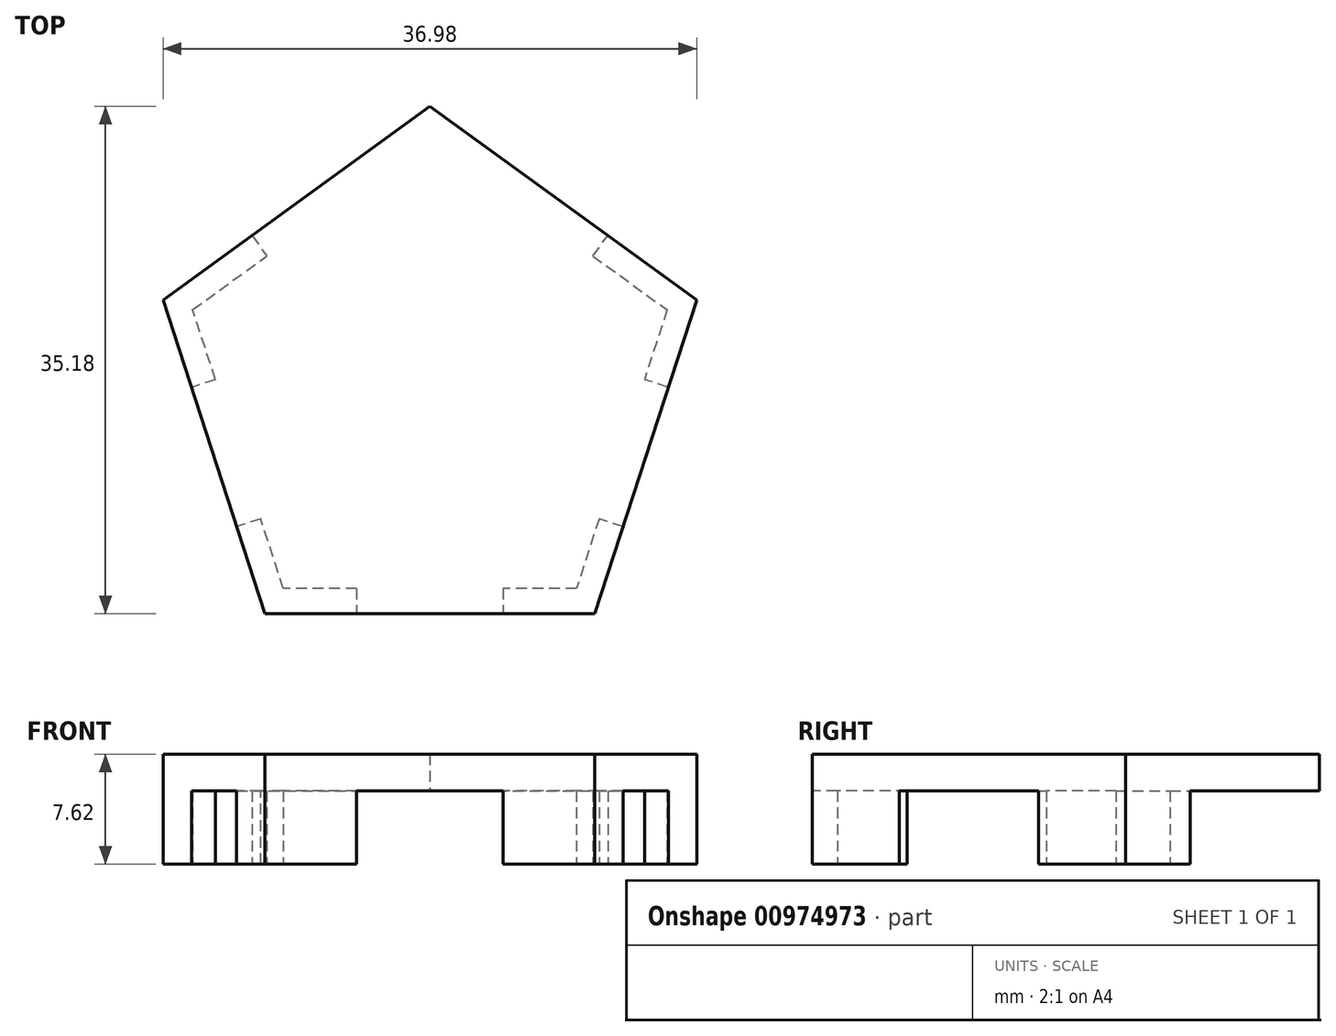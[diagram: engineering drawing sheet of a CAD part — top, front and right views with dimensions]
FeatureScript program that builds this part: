
annotation { "Feature Type Name" : "Feature", "Feature Type Description" : "" }
export const myFeature = defineFeature(function(context is Context, id is Id, definition is map)
    precondition{}
    {
        {
            var Q0;
            Q0=qCreatedBy(makeId("Top.planeOp"),FACE);
            var sketch = newSketch(context, id + "F0", { "sketchPlane" : qUnion([Q0])});
            skCircle(sketch, "E0.cCircle", {"center": v(0, 0) * mm, "radius": 19.45 * mm, "construction": true});
            skLineSegment(sketch, "E0.0", {"start": v(11.43, -15.73) * mm, "end": v(-11.43, -15.73) * mm});
            skLineSegment(sketch, "E0.1", {"start": v(-11.43, -15.73) * mm, "end": v(-18.5, 6) * mm});
            skLineSegment(sketch, "E0.2", {"start": v(-18.5, 6) * mm, "end": v(0, 19.45) * mm});
            skLineSegment(sketch, "E0.3", {"start": v(0, 19.45) * mm, "end": v(18.5, 6) * mm});
            skLineSegment(sketch, "E0.4", {"start": v(18.5, 6) * mm, "end": v(11.43, -15.73) * mm});
            skSolve(sketch);
        }
        {
            var Q0;
            Q0=makeQuery(id+"F0.imprint","IMPRINT",FACE,{"disambiguationData":[TD([[makeQuery(id+"F0.imprint","IMPRINT",EDGE,{"derivedFrom":sQuery(id+"F0.wireOp",EDGE,"E0.0")}),-1.0]])]});
            extrude(context, id + "F1", {"entities" : qUnion([Q0]), "depth" : 7.62 * mm, "offsetDistance" : 25.4 * mm});
        }
        {
            var Q0;
            Q0=qCreatedBy(makeId("Top.planeOp"),FACE);
            var sketch = newSketch(context, id + "F2", { "sketchPlane" : qUnion([Q0])});
            skCircle(sketch, "E1.cCircle", {"center": v(0, 0) * mm, "radius": 13.98 * mm, "construction": true});
            skLineSegment(sketch, "E1.0", {"start": v(16.44, 5.34) * mm, "end": v(10.16, -13.98) * mm});
            skLineSegment(sketch, "E1.1", {"start": v(10.16, -13.98) * mm, "end": v(-10.16, -13.98) * mm});
            skLineSegment(sketch, "E1.2", {"start": v(-10.16, -13.98) * mm, "end": v(-16.44, 5.34) * mm});
            skLineSegment(sketch, "E1.3", {"start": v(-16.44, 5.34) * mm, "end": v(0, 17.29) * mm});
            skLineSegment(sketch, "E1.4", {"start": v(0, 17.29) * mm, "end": v(16.44, 5.34) * mm});
            skPoint(sketch, "E1.0.midPoint", {"position": v(13.3, -4.32) * mm});
            skSolve(sketch);
        }
        {
            var Q0;
            Q0=qSketchRegion(id+"F2",true);
            extrude(context, id + "F3", {"entities" : qUnion([Q0]), "operationType" : NewBodyOperationType.REMOVE, "depth" : 5.08 * mm, "offsetDistance" : 25.4 * mm});
        }
        {
            var Q0;
            Q0=makeQuery(id+"F1.opExtrude","CAP_FACE",FACE,{"disambiguationData":[OSD([sQuery(id+"F0.wireOp",EDGE,"E0.0"),sQuery(id+"F0.wireOp",EDGE,"E0.1"),sQuery(id+"F0.wireOp",EDGE,"E0.2"),sQuery(id+"F0.wireOp",EDGE,"E0.3"),sQuery(id+"F0.wireOp",EDGE,"E0.4")])],"isStart":true});
            var sketch = newSketch(context, id + "F4", { "sketchPlane" : qUnion([Q0])});
            skLineSegment(sketch, "E2", {"start": v(0, 0) * mm, "end": v(23.62, 7.67) * mm});
            skLineSegment(sketch, "E3", {"start": v(0, 0) * mm, "end": v(-35.57, 11.56) * mm});
            skLineSegment(sketch, "E4", {"start": v(0, 0) * mm, "end": v(0, -28.1) * mm});
            skLineSegment(sketch, "E5.bottom", {"start": v(-11.25, -1.69) * mm, "end": v(-18.5, 0.67) * mm});
            skLineSegment(sketch, "E5.top", {"start": v(-8.1, 7.98) * mm, "end": v(-15.35, 10.33) * mm});
            skLineSegment(sketch, "E5.left", {"start": v(-11.25, -1.69) * mm, "end": v(-8.1, 7.98) * mm});
            skLineSegment(sketch, "E5.right", {"start": v(-18.5, 0.67) * mm, "end": v(-15.35, 10.33) * mm});
            skPoint(sketch, "E5.middle", {"position": v(-13.3, 4.32) * mm});
            skLineSegment(sketch, "E6.bottom", {"start": v(18.5, 0.67) * mm, "end": v(11.25, -1.69) * mm});
            skLineSegment(sketch, "E6.top", {"start": v(15.35, 10.33) * mm, "end": v(8.1, 7.98) * mm});
            skLineSegment(sketch, "E6.left", {"start": v(18.5, 0.67) * mm, "end": v(15.35, 10.33) * mm});
            skLineSegment(sketch, "E6.right", {"start": v(11.25, -1.69) * mm, "end": v(8.1, 7.98) * mm});
            skPoint(sketch, "E6.middle", {"position": v(13.3, 4.32) * mm});
            skLineSegment(sketch, "E7.bottom", {"start": v(5.08, 10.17) * mm, "end": v(-5.08, 10.17) * mm});
            skLineSegment(sketch, "E7.top", {"start": v(5.08, 17.8) * mm, "end": v(-5.08, 17.8) * mm});
            skLineSegment(sketch, "E7.left", {"start": v(5.08, 10.17) * mm, "end": v(5.08, 17.8) * mm});
            skLineSegment(sketch, "E7.right", {"start": v(-5.08, 10.17) * mm, "end": v(-5.08, 17.8) * mm});
            skPoint(sketch, "E7.middle", {"position": v(0, 13.98) * mm});
            skLineSegment(sketch, "E8", {"start": v(-12.33, -10.49) * mm, "end": v(-11.3, -9.07) * mm});
            skLineSegment(sketch, "E9", {"start": v(11.3, -9.07) * mm, "end": v(12.33, -10.49) * mm});
            skLineSegment(sketch, "E10", {"start": v(-11.3, -9.07) * mm, "end": v(11.3, -9.07) * mm});
            skLineSegment(sketch, "E11", {"start": v(-12.33, -10.49) * mm, "end": v(0, -28.1) * mm});
            skLineSegment(sketch, "E12", {"start": v(12.33, -10.49) * mm, "end": v(0, -28.1) * mm});
            skSolve(sketch);
        }
        {
            var Q0;
            {var subQ0=sQuery(id+"F4.wireOp",EDGE,"E3");var subQ1=makeQuery(id+"F3.boolean.opBoolean","COPY",EDGE,{"derivedFrom":makeQuery(id+"F3.opExtrude","CAP_EDGE",EDGE,{"disambiguationData":[OSD([sQuery(id+"F2.wireOp",EDGE,"E1.2")])],"isStart":true})});var subQ2=makeQuery(id+"F4.imprint","INTERSECT",VERTEX,{"derivedFrom":[subQ1,subQ0]});Q0=makeQuery(id+"F4.imprint","IMPRINT",FACE,{"disambiguationData":[TD([[makeQuery(id+"F4.imprint","IMPRINT",EDGE,{"disambiguationData":[TD([[subQ2,-1.0]])],"derivedFrom":subQ0}),1.0]])]});}
            var Q1;
            {var subQ0=sQuery(id+"F4.wireOp",EDGE,"E3");var subQ1=makeQuery(id+"F3.boolean.opBoolean","COPY",EDGE,{"derivedFrom":makeQuery(id+"F3.opExtrude","CAP_EDGE",EDGE,{"disambiguationData":[OSD([sQuery(id+"F2.wireOp",EDGE,"E1.2")])],"isStart":true})});var subQ2=makeQuery(id+"F4.imprint","INTERSECT",VERTEX,{"derivedFrom":[subQ1,subQ0]});Q1=makeQuery(id+"F4.imprint","IMPRINT",FACE,{"disambiguationData":[TD([[makeQuery(id+"F4.imprint","IMPRINT",EDGE,{"disambiguationData":[TD([[subQ2,-1.0]])],"derivedFrom":subQ0}),-1.0]])]});}
            var Q2;
            {var subQ0=sQuery(id+"F4.wireOp",EDGE,"E2");var subQ1=makeQuery(id+"F3.boolean.opBoolean","COPY",EDGE,{"derivedFrom":makeQuery(id+"F3.opExtrude","CAP_EDGE",EDGE,{"disambiguationData":[OSD([sQuery(id+"F2.wireOp",EDGE,"E1.0")])],"isStart":true})});var subQ2=makeQuery(id+"F4.imprint","INTERSECT",VERTEX,{"derivedFrom":[subQ1,subQ0]});Q2=makeQuery(id+"F4.imprint","IMPRINT",FACE,{"disambiguationData":[TD([[makeQuery(id+"F4.imprint","IMPRINT",EDGE,{"disambiguationData":[TD([[subQ2,-1.0]])],"derivedFrom":subQ0}),1.0]])]});}
            var Q3;
            {var subQ0=sQuery(id+"F4.wireOp",EDGE,"E2");var subQ1=makeQuery(id+"F3.boolean.opBoolean","COPY",EDGE,{"derivedFrom":makeQuery(id+"F3.opExtrude","CAP_EDGE",EDGE,{"disambiguationData":[OSD([sQuery(id+"F2.wireOp",EDGE,"E1.0")])],"isStart":true})});var subQ2=makeQuery(id+"F4.imprint","INTERSECT",VERTEX,{"derivedFrom":[subQ1,subQ0]});Q3=makeQuery(id+"F4.imprint","IMPRINT",FACE,{"disambiguationData":[TD([[makeQuery(id+"F4.imprint","IMPRINT",EDGE,{"disambiguationData":[TD([[subQ2,-1.0]])],"derivedFrom":subQ0}),-1.0]])]});}
            var Q4;
            {var subQ1=makeQuery(id+"F1.opExtrude","CAP_EDGE",EDGE,{"disambiguationData":[OSD([sQuery(id+"F0.wireOp",EDGE,"E0.2")])],"isStart":true});var subQ5=sQuery(id+"F4.wireOp",EDGE,"VIOiiu8y-qDuE-E9mX-nsSh-dz9hzi8E33ez.right");var subQ6=makeQuery(id+"F4.imprint","INTERSECT",VERTEX,{"derivedFrom":[subQ1,subQ5]});Q4=makeQuery(id+"F4.imprint","IMPRINT",FACE,{"disambiguationData":[TD([[makeQuery(id+"F4.imprint","IMPRINT",EDGE,{"disambiguationData":[TD([[subQ6,-1.0]])],"derivedFrom":subQ5}),-1.0]])]});}
            var Q5;
            {var subQ1=makeQuery(id+"F1.opExtrude","CAP_EDGE",EDGE,{"disambiguationData":[OSD([sQuery(id+"F0.wireOp",EDGE,"E0.3")])],"isStart":true});var subQ5=sQuery(id+"F4.wireOp",EDGE,"VIOiiu8y-qDuE-E9mX-nsSh-dz9hzi8E33ez.left");var subQ6=makeQuery(id+"F4.imprint","INTERSECT",VERTEX,{"derivedFrom":[subQ1,subQ5]});Q5=makeQuery(id+"F4.imprint","IMPRINT",FACE,{"disambiguationData":[TD([[makeQuery(id+"F4.imprint","IMPRINT",EDGE,{"disambiguationData":[TD([[subQ6,-1.0]])],"derivedFrom":subQ5}),1.0]])]});}
            var Q6;
            {var subQ0=sQuery(id+"F4.wireOp",EDGE,"E7.left");var subQ1=makeQuery(id+"F1.opExtrude","CAP_EDGE",EDGE,{"disambiguationData":[OSD([sQuery(id+"F0.wireOp",EDGE,"E0.0")])],"isStart":true});var subQ2=makeQuery(id+"F4.imprint","INTERSECT",VERTEX,{"derivedFrom":[subQ1,subQ0]});Q6=makeQuery(id+"F4.imprint","IMPRINT",FACE,{"disambiguationData":[TD([[makeQuery(id+"F4.imprint","IMPRINT",EDGE,{"disambiguationData":[TD([[subQ2,1.0]])],"derivedFrom":subQ0}),1.0]])]});}
            var Q7;
            {var subQ5=sQuery(id+"F4.wireOp",EDGE,"E8");Q7=makeQuery(id+"F4.imprint","IMPRINT",FACE,{"disambiguationData":[TD([[makeQuery(id+"F4.imprint","IMPRINT",EDGE,{"derivedFrom":subQ5}),-1.0]])]});}
            var Q8;
            {var subQ5=sQuery(id+"F4.wireOp",EDGE,"E9");Q8=makeQuery(id+"F4.imprint","IMPRINT",FACE,{"disambiguationData":[TD([[makeQuery(id+"F4.imprint","IMPRINT",EDGE,{"derivedFrom":subQ5}),-1.0]])]});}
            extrude(context, id + "F5", {"entities" : qUnion([Q0, Q1, Q2, Q3, Q4, Q5, Q6, Q7, Q8]), "operationType" : NewBodyOperationType.REMOVE, "oppositeDirection" : true, "depth" : 5.08 * mm, "offsetDistance" : 25.4 * mm});
        }
    });
